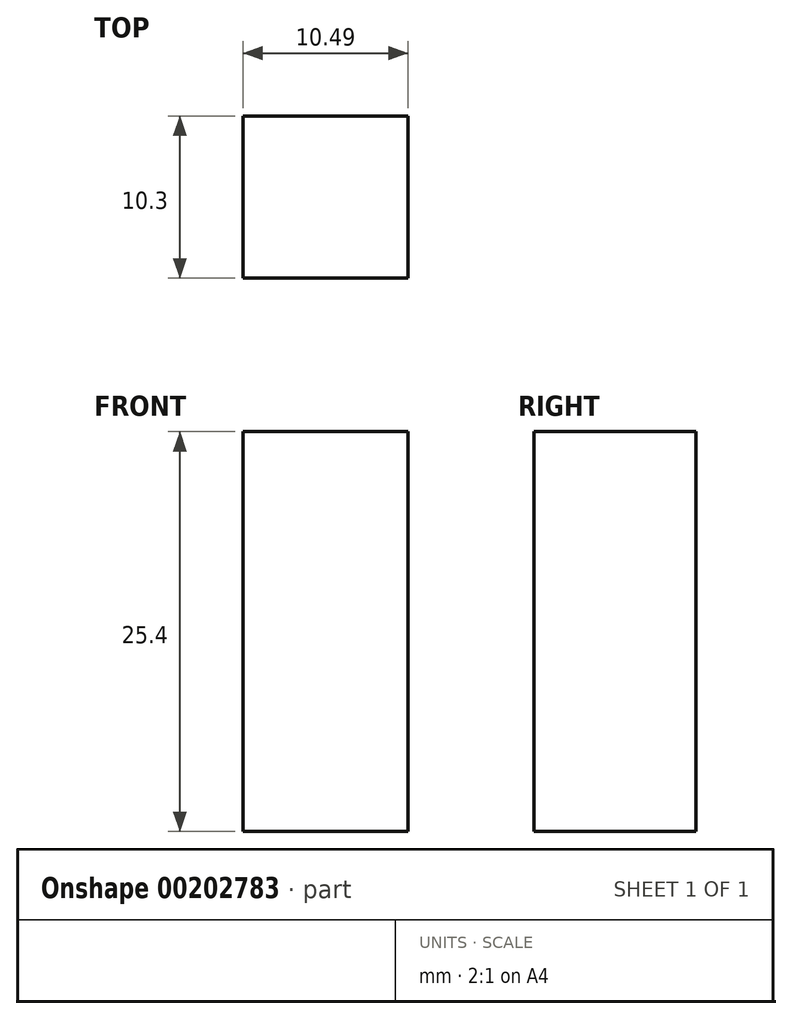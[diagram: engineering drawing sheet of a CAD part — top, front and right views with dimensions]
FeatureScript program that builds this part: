
annotation { "Feature Type Name" : "Feature", "Feature Type Description" : "" }
export const myFeature = defineFeature(function(context is Context, id is Id, definition is map)
    precondition{}
    {
        {
            var Q0;
            Q0=qCreatedBy(makeId("Top.planeOp"),FACE);
            var sketch = newSketch(context, id + "F0", { "sketchPlane" : qUnion([Q0])});
            skLineSegment(sketch, "E0", {"start": v(-5.15, 4.48) * mm, "end": v(-5.15, -5.82) * mm});
            skLineSegment(sketch, "E1", {"start": v(-5.15, 4.48) * mm, "end": v(5.34, 4.48) * mm});
            skLineSegment(sketch, "E2", {"start": v(5.34, 4.48) * mm, "end": v(5.34, -5.82) * mm});
            skLineSegment(sketch, "E3", {"start": v(-5.15, -5.82) * mm, "end": v(5.34, -5.82) * mm});
            skSolve(sketch);
        }
        {
            var Q0;
            Q0=makeQuery(id+"F0.imprint","IMPRINT",FACE,{"disambiguationData":[TD([[makeQuery(id+"F0.imprint","IMPRINT",EDGE,{"derivedFrom":sQuery(id+"F0.wireOp",EDGE,"E0")}),1.0]])]});
            extrude(context, id + "F1", {"entities" : qUnion([Q0]), "depth" : 25.4 * mm});
        }
    });
